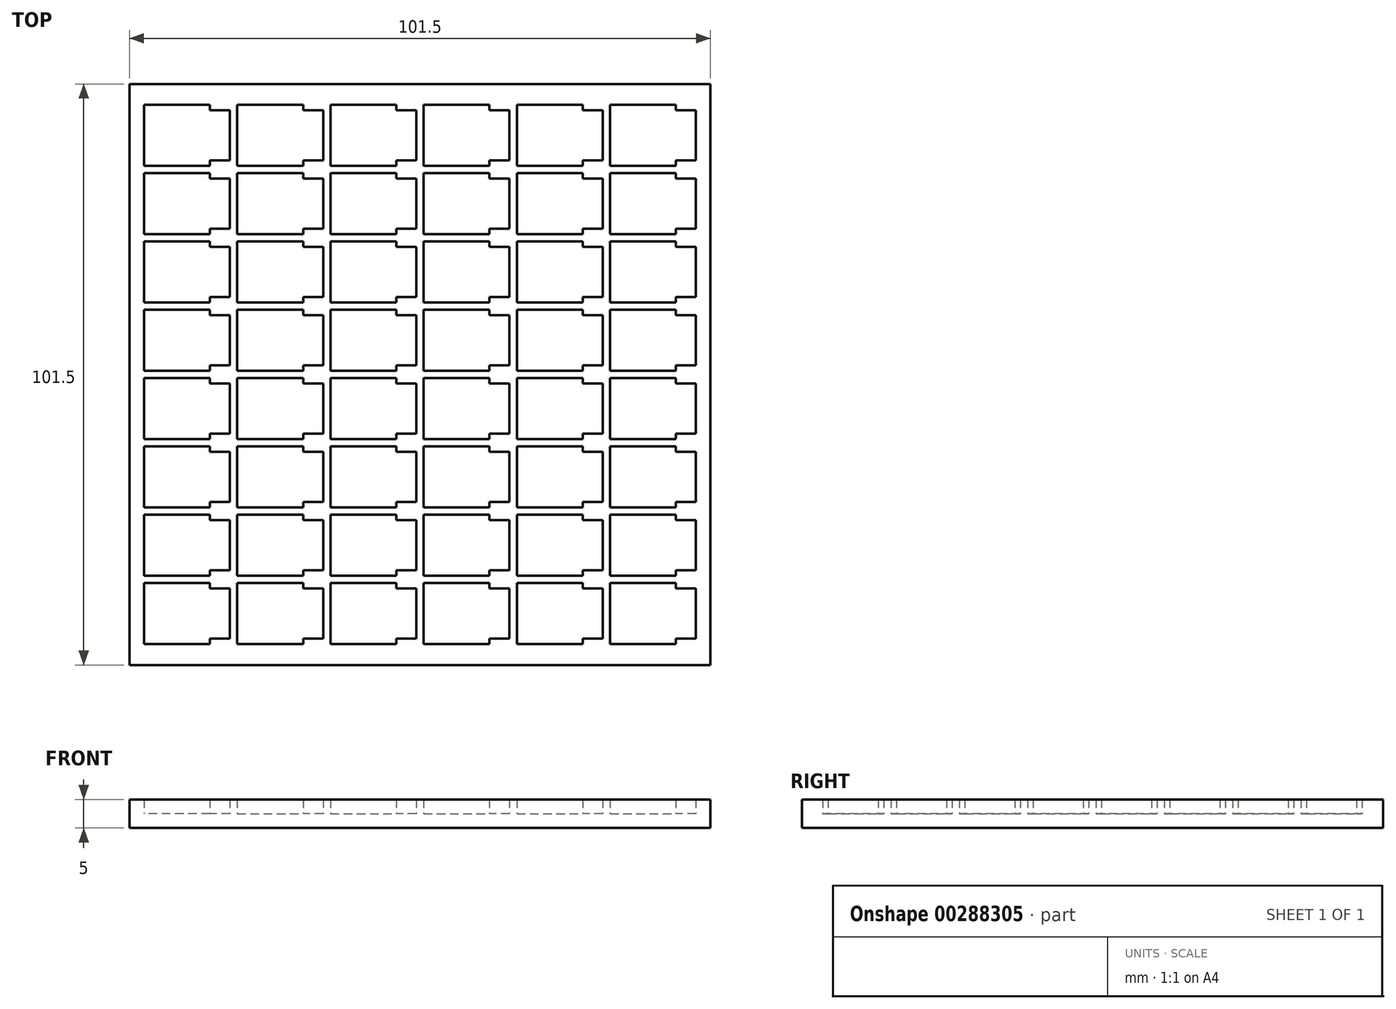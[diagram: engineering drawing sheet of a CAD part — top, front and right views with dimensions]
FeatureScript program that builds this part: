
annotation { "Feature Type Name" : "Feature", "Feature Type Description" : "" }
export const myFeature = defineFeature(function(context is Context, id is Id, definition is map)
    precondition{}
    {
        {
            var Q0;
            Q0=qCreatedBy(makeId("Top.planeOp"),FACE);
            var sketch = newSketch(context, id + "F0", { "sketchPlane" : qUnion([Q0])});
            skLineSegment(sketch, "E0.bottom", {"start": v(50.75, -50.75) * mm, "end": v(-50.75, -50.75) * mm});
            skLineSegment(sketch, "E0.top", {"start": v(50.75, 50.75) * mm, "end": v(-50.75, 50.75) * mm});
            skLineSegment(sketch, "E0.left", {"start": v(50.75, -50.75) * mm, "end": v(50.75, 50.75) * mm});
            skLineSegment(sketch, "E0.right", {"start": v(-50.75, -50.75) * mm, "end": v(-50.75, 50.75) * mm});
            skPoint(sketch, "E0.middle", {"position": v(0, 0) * mm});
            skLineSegment(sketch, "E1", {"start": v(-48.2, 47.12) * mm, "end": v(-48.2, 36.45) * mm});
            skLineSegment(sketch, "E2", {"start": v(-48.2, 36.45) * mm, "end": v(-36.7, 36.45) * mm});
            skLineSegment(sketch, "E3", {"start": v(-36.7, 36.45) * mm, "end": v(-36.7, 37.4) * mm});
            skLineSegment(sketch, "E4", {"start": v(-36.7, 37.4) * mm, "end": v(-33.2, 37.4) * mm});
            skLineSegment(sketch, "E5", {"start": v(-33.2, 37.4) * mm, "end": v(-33.2, 46.16) * mm});
            skLineSegment(sketch, "E6", {"start": v(-33.2, 46.16) * mm, "end": v(-36.7, 46.16) * mm});
            skLineSegment(sketch, "E7", {"start": v(-36.7, 46.16) * mm, "end": v(-36.7, 47.12) * mm});
            skLineSegment(sketch, "E8", {"start": v(-36.7, 47.12) * mm, "end": v(-48.2, 47.12) * mm});
            skLineSegment(sketch, "E9.0.1.0", {"start": v(-36.7, 24.5) * mm, "end": v(-36.7, 25.46) * mm});
            skLineSegment(sketch, "E9.0.1.1", {"start": v(-48.2, 24.5) * mm, "end": v(-36.7, 24.5) * mm});
            skLineSegment(sketch, "E9.0.1.2", {"start": v(-33.2, 25.46) * mm, "end": v(-33.2, 34.23) * mm});
            skLineSegment(sketch, "E9.0.1.3", {"start": v(-36.7, 34.23) * mm, "end": v(-36.7, 35.18) * mm});
            skLineSegment(sketch, "E9.0.1.4", {"start": v(-36.7, 25.46) * mm, "end": v(-33.2, 25.46) * mm});
            skLineSegment(sketch, "E9.0.1.5", {"start": v(-48.2, 35.18) * mm, "end": v(-48.2, 24.5) * mm});
            skLineSegment(sketch, "E9.0.1.6", {"start": v(-36.7, 35.18) * mm, "end": v(-48.2, 35.18) * mm});
            skLineSegment(sketch, "E9.0.1.7", {"start": v(-33.2, 34.23) * mm, "end": v(-36.7, 34.23) * mm});
            skLineSegment(sketch, "E9.0.2.0", {"start": v(-36.7, 12.57) * mm, "end": v(-36.7, 13.53) * mm});
            skLineSegment(sketch, "E9.0.2.1", {"start": v(-48.2, 12.57) * mm, "end": v(-36.7, 12.57) * mm});
            skLineSegment(sketch, "E9.0.2.2", {"start": v(-33.2, 13.53) * mm, "end": v(-33.2, 22.29) * mm});
            skLineSegment(sketch, "E9.0.2.3", {"start": v(-36.7, 22.29) * mm, "end": v(-36.7, 23.24) * mm});
            skLineSegment(sketch, "E9.0.2.4", {"start": v(-36.7, 13.53) * mm, "end": v(-33.2, 13.53) * mm});
            skLineSegment(sketch, "E9.0.2.5", {"start": v(-48.2, 23.24) * mm, "end": v(-48.2, 12.57) * mm});
            skLineSegment(sketch, "E9.0.2.6", {"start": v(-36.7, 23.24) * mm, "end": v(-48.2, 23.24) * mm});
            skLineSegment(sketch, "E9.0.2.7", {"start": v(-33.2, 22.29) * mm, "end": v(-36.7, 22.29) * mm});
            skLineSegment(sketch, "E9.0.3.0", {"start": v(-36.7, 0.63) * mm, "end": v(-36.7, 1.59) * mm});
            skLineSegment(sketch, "E9.0.3.1", {"start": v(-48.2, 0.63) * mm, "end": v(-36.7, 0.63) * mm});
            skLineSegment(sketch, "E9.0.3.2", {"start": v(-33.2, 1.59) * mm, "end": v(-33.2, 10.35) * mm});
            skLineSegment(sketch, "E9.0.3.3", {"start": v(-36.7, 10.35) * mm, "end": v(-36.7, 11.3) * mm});
            skLineSegment(sketch, "E9.0.3.4", {"start": v(-36.7, 1.59) * mm, "end": v(-33.2, 1.59) * mm});
            skLineSegment(sketch, "E9.0.3.5", {"start": v(-48.2, 11.3) * mm, "end": v(-48.2, 0.63) * mm});
            skLineSegment(sketch, "E9.0.3.6", {"start": v(-36.7, 11.3) * mm, "end": v(-48.2, 11.3) * mm});
            skLineSegment(sketch, "E9.0.3.7", {"start": v(-33.2, 10.35) * mm, "end": v(-36.7, 10.35) * mm});
            skLineSegment(sketch, "E9.0.4.0", {"start": v(-36.7, -11.3) * mm, "end": v(-36.7, -10.35) * mm});
            skLineSegment(sketch, "E9.0.4.1", {"start": v(-48.2, -11.3) * mm, "end": v(-36.7, -11.3) * mm});
            skLineSegment(sketch, "E9.0.4.2", {"start": v(-33.2, -10.35) * mm, "end": v(-33.2, -1.59) * mm});
            skLineSegment(sketch, "E9.0.4.3", {"start": v(-36.7, -1.59) * mm, "end": v(-36.7, -0.63) * mm});
            skLineSegment(sketch, "E9.0.4.4", {"start": v(-36.7, -10.35) * mm, "end": v(-33.2, -10.35) * mm});
            skLineSegment(sketch, "E9.0.4.5", {"start": v(-48.2, -0.63) * mm, "end": v(-48.2, -11.3) * mm});
            skLineSegment(sketch, "E9.0.4.6", {"start": v(-36.7, -0.63) * mm, "end": v(-48.2, -0.63) * mm});
            skLineSegment(sketch, "E9.0.4.7", {"start": v(-33.2, -1.59) * mm, "end": v(-36.7, -1.59) * mm});
            skLineSegment(sketch, "E9.0.5.0", {"start": v(-36.7, -23.24) * mm, "end": v(-36.7, -22.29) * mm});
            skLineSegment(sketch, "E9.0.5.1", {"start": v(-48.2, -23.24) * mm, "end": v(-36.7, -23.24) * mm});
            skLineSegment(sketch, "E9.0.5.2", {"start": v(-33.2, -22.29) * mm, "end": v(-33.2, -13.53) * mm});
            skLineSegment(sketch, "E9.0.5.3", {"start": v(-36.7, -13.53) * mm, "end": v(-36.7, -12.57) * mm});
            skLineSegment(sketch, "E9.0.5.4", {"start": v(-36.7, -22.29) * mm, "end": v(-33.2, -22.29) * mm});
            skLineSegment(sketch, "E9.0.5.5", {"start": v(-48.2, -12.57) * mm, "end": v(-48.2, -23.24) * mm});
            skLineSegment(sketch, "E9.0.5.6", {"start": v(-36.7, -12.57) * mm, "end": v(-48.2, -12.57) * mm});
            skLineSegment(sketch, "E9.0.5.7", {"start": v(-33.2, -13.53) * mm, "end": v(-36.7, -13.53) * mm});
            skLineSegment(sketch, "E9.0.6.0", {"start": v(-36.7, -35.18) * mm, "end": v(-36.7, -34.23) * mm});
            skLineSegment(sketch, "E9.0.6.1", {"start": v(-48.2, -35.18) * mm, "end": v(-36.7, -35.18) * mm});
            skLineSegment(sketch, "E9.0.6.2", {"start": v(-33.2, -34.23) * mm, "end": v(-33.2, -25.46) * mm});
            skLineSegment(sketch, "E9.0.6.3", {"start": v(-36.7, -25.46) * mm, "end": v(-36.7, -24.51) * mm});
            skLineSegment(sketch, "E9.0.6.4", {"start": v(-36.7, -34.23) * mm, "end": v(-33.2, -34.23) * mm});
            skLineSegment(sketch, "E9.0.6.5", {"start": v(-48.2, -24.51) * mm, "end": v(-48.2, -35.18) * mm});
            skLineSegment(sketch, "E9.0.6.6", {"start": v(-36.7, -24.51) * mm, "end": v(-48.2, -24.51) * mm});
            skLineSegment(sketch, "E9.0.6.7", {"start": v(-33.2, -25.46) * mm, "end": v(-36.7, -25.46) * mm});
            skLineSegment(sketch, "E9.0.7.0", {"start": v(-36.7, -47.12) * mm, "end": v(-36.7, -46.16) * mm});
            skLineSegment(sketch, "E9.0.7.1", {"start": v(-48.2, -47.12) * mm, "end": v(-36.7, -47.12) * mm});
            skLineSegment(sketch, "E9.0.7.2", {"start": v(-33.2, -46.16) * mm, "end": v(-33.2, -37.4) * mm});
            skLineSegment(sketch, "E9.0.7.3", {"start": v(-36.7, -37.4) * mm, "end": v(-36.7, -36.45) * mm});
            skLineSegment(sketch, "E9.0.7.4", {"start": v(-36.7, -46.16) * mm, "end": v(-33.2, -46.16) * mm});
            skLineSegment(sketch, "E9.0.7.5", {"start": v(-48.2, -36.45) * mm, "end": v(-48.2, -47.12) * mm});
            skLineSegment(sketch, "E9.0.7.6", {"start": v(-36.7, -36.45) * mm, "end": v(-48.2, -36.45) * mm});
            skLineSegment(sketch, "E9.0.7.7", {"start": v(-33.2, -37.4) * mm, "end": v(-36.7, -37.4) * mm});
            skLineSegment(sketch, "E9.1.0.0", {"start": v(-20.42, 36.45) * mm, "end": v(-20.42, 37.4) * mm});
            skLineSegment(sketch, "E9.1.0.1", {"start": v(-31.92, 36.45) * mm, "end": v(-20.42, 36.45) * mm});
            skLineSegment(sketch, "E9.1.0.2", {"start": v(-16.92, 37.4) * mm, "end": v(-16.92, 46.16) * mm});
            skLineSegment(sketch, "E9.1.0.3", {"start": v(-20.42, 46.16) * mm, "end": v(-20.42, 47.12) * mm});
            skLineSegment(sketch, "E9.1.0.4", {"start": v(-20.42, 37.4) * mm, "end": v(-16.92, 37.4) * mm});
            skLineSegment(sketch, "E9.1.0.5", {"start": v(-31.92, 47.12) * mm, "end": v(-31.92, 36.45) * mm});
            skLineSegment(sketch, "E9.1.0.6", {"start": v(-20.42, 47.12) * mm, "end": v(-31.92, 47.12) * mm});
            skLineSegment(sketch, "E9.1.0.7", {"start": v(-16.92, 46.16) * mm, "end": v(-20.42, 46.16) * mm});
            skLineSegment(sketch, "E9.1.1.0", {"start": v(-20.42, 24.5) * mm, "end": v(-20.42, 25.46) * mm});
            skLineSegment(sketch, "E9.1.1.1", {"start": v(-31.92, 24.5) * mm, "end": v(-20.42, 24.5) * mm});
            skLineSegment(sketch, "E9.1.1.2", {"start": v(-16.92, 25.46) * mm, "end": v(-16.92, 34.23) * mm});
            skLineSegment(sketch, "E9.1.1.3", {"start": v(-20.42, 34.23) * mm, "end": v(-20.42, 35.18) * mm});
            skLineSegment(sketch, "E9.1.1.4", {"start": v(-20.42, 25.46) * mm, "end": v(-16.92, 25.46) * mm});
            skLineSegment(sketch, "E9.1.1.5", {"start": v(-31.92, 35.18) * mm, "end": v(-31.92, 24.5) * mm});
            skLineSegment(sketch, "E9.1.1.6", {"start": v(-20.42, 35.18) * mm, "end": v(-31.92, 35.18) * mm});
            skLineSegment(sketch, "E9.1.1.7", {"start": v(-16.92, 34.23) * mm, "end": v(-20.42, 34.23) * mm});
            skLineSegment(sketch, "E9.1.2.0", {"start": v(-20.42, 12.57) * mm, "end": v(-20.42, 13.53) * mm});
            skLineSegment(sketch, "E9.1.2.1", {"start": v(-31.92, 12.57) * mm, "end": v(-20.42, 12.57) * mm});
            skLineSegment(sketch, "E9.1.2.2", {"start": v(-16.92, 13.53) * mm, "end": v(-16.92, 22.29) * mm});
            skLineSegment(sketch, "E9.1.2.3", {"start": v(-20.42, 22.29) * mm, "end": v(-20.42, 23.24) * mm});
            skLineSegment(sketch, "E9.1.2.4", {"start": v(-20.42, 13.53) * mm, "end": v(-16.92, 13.53) * mm});
            skLineSegment(sketch, "E9.1.2.5", {"start": v(-31.92, 23.24) * mm, "end": v(-31.92, 12.57) * mm});
            skLineSegment(sketch, "E9.1.2.6", {"start": v(-20.42, 23.24) * mm, "end": v(-31.92, 23.24) * mm});
            skLineSegment(sketch, "E9.1.2.7", {"start": v(-16.92, 22.29) * mm, "end": v(-20.42, 22.29) * mm});
            skLineSegment(sketch, "E9.1.3.0", {"start": v(-20.42, 0.63) * mm, "end": v(-20.42, 1.59) * mm});
            skLineSegment(sketch, "E9.1.3.1", {"start": v(-31.92, 0.63) * mm, "end": v(-20.42, 0.63) * mm});
            skLineSegment(sketch, "E9.1.3.2", {"start": v(-16.92, 1.59) * mm, "end": v(-16.92, 10.35) * mm});
            skLineSegment(sketch, "E9.1.3.3", {"start": v(-20.42, 10.35) * mm, "end": v(-20.42, 11.3) * mm});
            skLineSegment(sketch, "E9.1.3.4", {"start": v(-20.42, 1.59) * mm, "end": v(-16.92, 1.59) * mm});
            skLineSegment(sketch, "E9.1.3.5", {"start": v(-31.92, 11.3) * mm, "end": v(-31.92, 0.63) * mm});
            skLineSegment(sketch, "E9.1.3.6", {"start": v(-20.42, 11.3) * mm, "end": v(-31.92, 11.3) * mm});
            skLineSegment(sketch, "E9.1.3.7", {"start": v(-16.92, 10.35) * mm, "end": v(-20.42, 10.35) * mm});
            skLineSegment(sketch, "E9.1.4.0", {"start": v(-20.42, -11.3) * mm, "end": v(-20.42, -10.35) * mm});
            skLineSegment(sketch, "E9.1.4.1", {"start": v(-31.92, -11.3) * mm, "end": v(-20.42, -11.3) * mm});
            skLineSegment(sketch, "E9.1.4.2", {"start": v(-16.92, -10.35) * mm, "end": v(-16.92, -1.59) * mm});
            skLineSegment(sketch, "E9.1.4.3", {"start": v(-20.42, -1.59) * mm, "end": v(-20.42, -0.63) * mm});
            skLineSegment(sketch, "E9.1.4.4", {"start": v(-20.42, -10.35) * mm, "end": v(-16.92, -10.35) * mm});
            skLineSegment(sketch, "E9.1.4.5", {"start": v(-31.92, -0.63) * mm, "end": v(-31.92, -11.3) * mm});
            skLineSegment(sketch, "E9.1.4.6", {"start": v(-20.42, -0.63) * mm, "end": v(-31.92, -0.63) * mm});
            skLineSegment(sketch, "E9.1.4.7", {"start": v(-16.92, -1.59) * mm, "end": v(-20.42, -1.59) * mm});
            skLineSegment(sketch, "E9.1.5.0", {"start": v(-20.42, -23.24) * mm, "end": v(-20.42, -22.29) * mm});
            skLineSegment(sketch, "E9.1.5.1", {"start": v(-31.92, -23.24) * mm, "end": v(-20.42, -23.24) * mm});
            skLineSegment(sketch, "E9.1.5.2", {"start": v(-16.92, -22.29) * mm, "end": v(-16.92, -13.53) * mm});
            skLineSegment(sketch, "E9.1.5.3", {"start": v(-20.42, -13.53) * mm, "end": v(-20.42, -12.57) * mm});
            skLineSegment(sketch, "E9.1.5.4", {"start": v(-20.42, -22.29) * mm, "end": v(-16.92, -22.29) * mm});
            skLineSegment(sketch, "E9.1.5.5", {"start": v(-31.92, -12.57) * mm, "end": v(-31.92, -23.24) * mm});
            skLineSegment(sketch, "E9.1.5.6", {"start": v(-20.42, -12.57) * mm, "end": v(-31.92, -12.57) * mm});
            skLineSegment(sketch, "E9.1.5.7", {"start": v(-16.92, -13.53) * mm, "end": v(-20.42, -13.53) * mm});
            skLineSegment(sketch, "E9.1.6.0", {"start": v(-20.42, -35.18) * mm, "end": v(-20.42, -34.23) * mm});
            skLineSegment(sketch, "E9.1.6.1", {"start": v(-31.92, -35.18) * mm, "end": v(-20.42, -35.18) * mm});
            skLineSegment(sketch, "E9.1.6.2", {"start": v(-16.92, -34.23) * mm, "end": v(-16.92, -25.46) * mm});
            skLineSegment(sketch, "E9.1.6.3", {"start": v(-20.42, -25.46) * mm, "end": v(-20.42, -24.51) * mm});
            skLineSegment(sketch, "E9.1.6.4", {"start": v(-20.42, -34.23) * mm, "end": v(-16.92, -34.23) * mm});
            skLineSegment(sketch, "E9.1.6.5", {"start": v(-31.92, -24.51) * mm, "end": v(-31.92, -35.18) * mm});
            skLineSegment(sketch, "E9.1.6.6", {"start": v(-20.42, -24.51) * mm, "end": v(-31.92, -24.51) * mm});
            skLineSegment(sketch, "E9.1.6.7", {"start": v(-16.92, -25.46) * mm, "end": v(-20.42, -25.46) * mm});
            skLineSegment(sketch, "E9.1.7.0", {"start": v(-20.42, -47.12) * mm, "end": v(-20.42, -46.16) * mm});
            skLineSegment(sketch, "E9.1.7.1", {"start": v(-31.92, -47.12) * mm, "end": v(-20.42, -47.12) * mm});
            skLineSegment(sketch, "E9.1.7.2", {"start": v(-16.92, -46.16) * mm, "end": v(-16.92, -37.4) * mm});
            skLineSegment(sketch, "E9.1.7.3", {"start": v(-20.42, -37.4) * mm, "end": v(-20.42, -36.45) * mm});
            skLineSegment(sketch, "E9.1.7.4", {"start": v(-20.42, -46.16) * mm, "end": v(-16.92, -46.16) * mm});
            skLineSegment(sketch, "E9.1.7.5", {"start": v(-31.92, -36.45) * mm, "end": v(-31.92, -47.12) * mm});
            skLineSegment(sketch, "E9.1.7.6", {"start": v(-20.42, -36.45) * mm, "end": v(-31.92, -36.45) * mm});
            skLineSegment(sketch, "E9.1.7.7", {"start": v(-16.92, -37.4) * mm, "end": v(-20.42, -37.4) * mm});
            skLineSegment(sketch, "E9.2.0.0", {"start": v(-4.13, 36.45) * mm, "end": v(-4.13, 37.4) * mm});
            skLineSegment(sketch, "E9.2.0.1", {"start": v(-15.63, 36.45) * mm, "end": v(-4.13, 36.45) * mm});
            skLineSegment(sketch, "E9.2.0.2", {"start": v(-0.63, 37.4) * mm, "end": v(-0.63, 46.16) * mm});
            skLineSegment(sketch, "E9.2.0.3", {"start": v(-4.13, 46.16) * mm, "end": v(-4.13, 47.12) * mm});
            skLineSegment(sketch, "E9.2.0.4", {"start": v(-4.13, 37.4) * mm, "end": v(-0.63, 37.4) * mm});
            skLineSegment(sketch, "E9.2.0.5", {"start": v(-15.63, 47.12) * mm, "end": v(-15.63, 36.45) * mm});
            skLineSegment(sketch, "E9.2.0.6", {"start": v(-4.13, 47.12) * mm, "end": v(-15.63, 47.12) * mm});
            skLineSegment(sketch, "E9.2.0.7", {"start": v(-0.63, 46.16) * mm, "end": v(-4.13, 46.16) * mm});
            skLineSegment(sketch, "E9.2.1.0", {"start": v(-4.13, 24.5) * mm, "end": v(-4.13, 25.46) * mm});
            skLineSegment(sketch, "E9.2.1.1", {"start": v(-15.63, 24.5) * mm, "end": v(-4.13, 24.5) * mm});
            skLineSegment(sketch, "E9.2.1.2", {"start": v(-0.63, 25.46) * mm, "end": v(-0.63, 34.23) * mm});
            skLineSegment(sketch, "E9.2.1.3", {"start": v(-4.13, 34.23) * mm, "end": v(-4.13, 35.18) * mm});
            skLineSegment(sketch, "E9.2.1.4", {"start": v(-4.13, 25.46) * mm, "end": v(-0.63, 25.46) * mm});
            skLineSegment(sketch, "E9.2.1.5", {"start": v(-15.63, 35.18) * mm, "end": v(-15.63, 24.5) * mm});
            skLineSegment(sketch, "E9.2.1.6", {"start": v(-4.13, 35.18) * mm, "end": v(-15.63, 35.18) * mm});
            skLineSegment(sketch, "E9.2.1.7", {"start": v(-0.63, 34.23) * mm, "end": v(-4.13, 34.23) * mm});
            skLineSegment(sketch, "E9.2.2.0", {"start": v(-4.13, 12.57) * mm, "end": v(-4.13, 13.53) * mm});
            skLineSegment(sketch, "E9.2.2.1", {"start": v(-15.63, 12.57) * mm, "end": v(-4.13, 12.57) * mm});
            skLineSegment(sketch, "E9.2.2.2", {"start": v(-0.63, 13.53) * mm, "end": v(-0.63, 22.29) * mm});
            skLineSegment(sketch, "E9.2.2.3", {"start": v(-4.13, 22.29) * mm, "end": v(-4.13, 23.24) * mm});
            skLineSegment(sketch, "E9.2.2.4", {"start": v(-4.13, 13.53) * mm, "end": v(-0.63, 13.53) * mm});
            skLineSegment(sketch, "E9.2.2.5", {"start": v(-15.63, 23.24) * mm, "end": v(-15.63, 12.57) * mm});
            skLineSegment(sketch, "E9.2.2.6", {"start": v(-4.13, 23.24) * mm, "end": v(-15.63, 23.24) * mm});
            skLineSegment(sketch, "E9.2.2.7", {"start": v(-0.63, 22.29) * mm, "end": v(-4.13, 22.29) * mm});
            skLineSegment(sketch, "E9.2.3.0", {"start": v(-4.13, 0.63) * mm, "end": v(-4.13, 1.59) * mm});
            skLineSegment(sketch, "E9.2.3.1", {"start": v(-15.63, 0.63) * mm, "end": v(-4.13, 0.63) * mm});
            skLineSegment(sketch, "E9.2.3.2", {"start": v(-0.63, 1.59) * mm, "end": v(-0.63, 10.35) * mm});
            skLineSegment(sketch, "E9.2.3.3", {"start": v(-4.13, 10.35) * mm, "end": v(-4.13, 11.3) * mm});
            skLineSegment(sketch, "E9.2.3.4", {"start": v(-4.13, 1.59) * mm, "end": v(-0.63, 1.59) * mm});
            skLineSegment(sketch, "E9.2.3.5", {"start": v(-15.63, 11.3) * mm, "end": v(-15.63, 0.63) * mm});
            skLineSegment(sketch, "E9.2.3.6", {"start": v(-4.13, 11.3) * mm, "end": v(-15.63, 11.3) * mm});
            skLineSegment(sketch, "E9.2.3.7", {"start": v(-0.63, 10.35) * mm, "end": v(-4.13, 10.35) * mm});
            skLineSegment(sketch, "E9.2.4.0", {"start": v(-4.13, -11.3) * mm, "end": v(-4.13, -10.35) * mm});
            skLineSegment(sketch, "E9.2.4.1", {"start": v(-15.63, -11.3) * mm, "end": v(-4.13, -11.3) * mm});
            skLineSegment(sketch, "E9.2.4.2", {"start": v(-0.63, -10.35) * mm, "end": v(-0.63, -1.59) * mm});
            skLineSegment(sketch, "E9.2.4.3", {"start": v(-4.13, -1.59) * mm, "end": v(-4.13, -0.63) * mm});
            skLineSegment(sketch, "E9.2.4.4", {"start": v(-4.13, -10.35) * mm, "end": v(-0.63, -10.35) * mm});
            skLineSegment(sketch, "E9.2.4.5", {"start": v(-15.63, -0.63) * mm, "end": v(-15.63, -11.3) * mm});
            skLineSegment(sketch, "E9.2.4.6", {"start": v(-4.13, -0.63) * mm, "end": v(-15.63, -0.63) * mm});
            skLineSegment(sketch, "E9.2.4.7", {"start": v(-0.63, -1.59) * mm, "end": v(-4.13, -1.59) * mm});
            skLineSegment(sketch, "E9.2.5.0", {"start": v(-4.13, -23.24) * mm, "end": v(-4.13, -22.29) * mm});
            skLineSegment(sketch, "E9.2.5.1", {"start": v(-15.63, -23.24) * mm, "end": v(-4.13, -23.24) * mm});
            skLineSegment(sketch, "E9.2.5.2", {"start": v(-0.63, -22.29) * mm, "end": v(-0.63, -13.53) * mm});
            skLineSegment(sketch, "E9.2.5.3", {"start": v(-4.13, -13.53) * mm, "end": v(-4.13, -12.57) * mm});
            skLineSegment(sketch, "E9.2.5.4", {"start": v(-4.13, -22.29) * mm, "end": v(-0.63, -22.29) * mm});
            skLineSegment(sketch, "E9.2.5.5", {"start": v(-15.63, -12.57) * mm, "end": v(-15.63, -23.24) * mm});
            skLineSegment(sketch, "E9.2.5.6", {"start": v(-4.13, -12.57) * mm, "end": v(-15.63, -12.57) * mm});
            skLineSegment(sketch, "E9.2.5.7", {"start": v(-0.63, -13.53) * mm, "end": v(-4.13, -13.53) * mm});
            skLineSegment(sketch, "E9.2.6.0", {"start": v(-4.13, -35.18) * mm, "end": v(-4.13, -34.23) * mm});
            skLineSegment(sketch, "E9.2.6.1", {"start": v(-15.63, -35.18) * mm, "end": v(-4.13, -35.18) * mm});
            skLineSegment(sketch, "E9.2.6.2", {"start": v(-0.63, -34.23) * mm, "end": v(-0.63, -25.46) * mm});
            skLineSegment(sketch, "E9.2.6.3", {"start": v(-4.13, -25.46) * mm, "end": v(-4.13, -24.51) * mm});
            skLineSegment(sketch, "E9.2.6.4", {"start": v(-4.13, -34.23) * mm, "end": v(-0.63, -34.23) * mm});
            skLineSegment(sketch, "E9.2.6.5", {"start": v(-15.63, -24.51) * mm, "end": v(-15.63, -35.18) * mm});
            skLineSegment(sketch, "E9.2.6.6", {"start": v(-4.13, -24.51) * mm, "end": v(-15.63, -24.51) * mm});
            skLineSegment(sketch, "E9.2.6.7", {"start": v(-0.63, -25.46) * mm, "end": v(-4.13, -25.46) * mm});
            skLineSegment(sketch, "E9.2.7.0", {"start": v(-4.13, -47.12) * mm, "end": v(-4.13, -46.16) * mm});
            skLineSegment(sketch, "E9.2.7.1", {"start": v(-15.63, -47.12) * mm, "end": v(-4.13, -47.12) * mm});
            skLineSegment(sketch, "E9.2.7.2", {"start": v(-0.63, -46.16) * mm, "end": v(-0.63, -37.4) * mm});
            skLineSegment(sketch, "E9.2.7.3", {"start": v(-4.13, -37.4) * mm, "end": v(-4.13, -36.45) * mm});
            skLineSegment(sketch, "E9.2.7.4", {"start": v(-4.13, -46.16) * mm, "end": v(-0.63, -46.16) * mm});
            skLineSegment(sketch, "E9.2.7.5", {"start": v(-15.63, -36.45) * mm, "end": v(-15.63, -47.12) * mm});
            skLineSegment(sketch, "E9.2.7.6", {"start": v(-4.13, -36.45) * mm, "end": v(-15.63, -36.45) * mm});
            skLineSegment(sketch, "E9.2.7.7", {"start": v(-0.63, -37.4) * mm, "end": v(-4.13, -37.4) * mm});
            skLineSegment(sketch, "E9.3.0.0", {"start": v(12.15, 36.45) * mm, "end": v(12.15, 37.4) * mm});
            skLineSegment(sketch, "E9.3.0.1", {"start": v(0.65, 36.45) * mm, "end": v(12.15, 36.45) * mm});
            skLineSegment(sketch, "E9.3.0.2", {"start": v(15.65, 37.4) * mm, "end": v(15.65, 46.16) * mm});
            skLineSegment(sketch, "E9.3.0.3", {"start": v(12.15, 46.16) * mm, "end": v(12.15, 47.12) * mm});
            skLineSegment(sketch, "E9.3.0.4", {"start": v(12.15, 37.4) * mm, "end": v(15.65, 37.4) * mm});
            skLineSegment(sketch, "E9.3.0.5", {"start": v(0.65, 47.12) * mm, "end": v(0.65, 36.45) * mm});
            skLineSegment(sketch, "E9.3.0.6", {"start": v(12.15, 47.12) * mm, "end": v(0.65, 47.12) * mm});
            skLineSegment(sketch, "E9.3.0.7", {"start": v(15.65, 46.16) * mm, "end": v(12.15, 46.16) * mm});
            skLineSegment(sketch, "E9.3.1.0", {"start": v(12.15, 24.5) * mm, "end": v(12.15, 25.46) * mm});
            skLineSegment(sketch, "E9.3.1.1", {"start": v(0.65, 24.5) * mm, "end": v(12.15, 24.5) * mm});
            skLineSegment(sketch, "E9.3.1.2", {"start": v(15.65, 25.46) * mm, "end": v(15.65, 34.23) * mm});
            skLineSegment(sketch, "E9.3.1.3", {"start": v(12.15, 34.23) * mm, "end": v(12.15, 35.18) * mm});
            skLineSegment(sketch, "E9.3.1.4", {"start": v(12.15, 25.46) * mm, "end": v(15.65, 25.46) * mm});
            skLineSegment(sketch, "E9.3.1.5", {"start": v(0.65, 35.18) * mm, "end": v(0.65, 24.5) * mm});
            skLineSegment(sketch, "E9.3.1.6", {"start": v(12.15, 35.18) * mm, "end": v(0.65, 35.18) * mm});
            skLineSegment(sketch, "E9.3.1.7", {"start": v(15.65, 34.23) * mm, "end": v(12.15, 34.23) * mm});
            skLineSegment(sketch, "E9.3.2.0", {"start": v(12.15, 12.57) * mm, "end": v(12.15, 13.53) * mm});
            skLineSegment(sketch, "E9.3.2.1", {"start": v(0.65, 12.57) * mm, "end": v(12.15, 12.57) * mm});
            skLineSegment(sketch, "E9.3.2.2", {"start": v(15.65, 13.53) * mm, "end": v(15.65, 22.29) * mm});
            skLineSegment(sketch, "E9.3.2.3", {"start": v(12.15, 22.29) * mm, "end": v(12.15, 23.24) * mm});
            skLineSegment(sketch, "E9.3.2.4", {"start": v(12.15, 13.53) * mm, "end": v(15.65, 13.53) * mm});
            skLineSegment(sketch, "E9.3.2.5", {"start": v(0.65, 23.24) * mm, "end": v(0.65, 12.57) * mm});
            skLineSegment(sketch, "E9.3.2.6", {"start": v(12.15, 23.24) * mm, "end": v(0.65, 23.24) * mm});
            skLineSegment(sketch, "E9.3.2.7", {"start": v(15.65, 22.29) * mm, "end": v(12.15, 22.29) * mm});
            skLineSegment(sketch, "E9.3.3.0", {"start": v(12.15, 0.63) * mm, "end": v(12.15, 1.59) * mm});
            skLineSegment(sketch, "E9.3.3.1", {"start": v(0.65, 0.63) * mm, "end": v(12.15, 0.63) * mm});
            skLineSegment(sketch, "E9.3.3.2", {"start": v(15.65, 1.59) * mm, "end": v(15.65, 10.35) * mm});
            skLineSegment(sketch, "E9.3.3.3", {"start": v(12.15, 10.35) * mm, "end": v(12.15, 11.3) * mm});
            skLineSegment(sketch, "E9.3.3.4", {"start": v(12.15, 1.59) * mm, "end": v(15.65, 1.59) * mm});
            skLineSegment(sketch, "E9.3.3.5", {"start": v(0.65, 11.3) * mm, "end": v(0.65, 0.63) * mm});
            skLineSegment(sketch, "E9.3.3.6", {"start": v(12.15, 11.3) * mm, "end": v(0.65, 11.3) * mm});
            skLineSegment(sketch, "E9.3.3.7", {"start": v(15.65, 10.35) * mm, "end": v(12.15, 10.35) * mm});
            skLineSegment(sketch, "E9.3.4.0", {"start": v(12.15, -11.3) * mm, "end": v(12.15, -10.35) * mm});
            skLineSegment(sketch, "E9.3.4.1", {"start": v(0.65, -11.3) * mm, "end": v(12.15, -11.3) * mm});
            skLineSegment(sketch, "E9.3.4.2", {"start": v(15.65, -10.35) * mm, "end": v(15.65, -1.59) * mm});
            skLineSegment(sketch, "E9.3.4.3", {"start": v(12.15, -1.59) * mm, "end": v(12.15, -0.63) * mm});
            skLineSegment(sketch, "E9.3.4.4", {"start": v(12.15, -10.35) * mm, "end": v(15.65, -10.35) * mm});
            skLineSegment(sketch, "E9.3.4.5", {"start": v(0.65, -0.63) * mm, "end": v(0.65, -11.3) * mm});
            skLineSegment(sketch, "E9.3.4.6", {"start": v(12.15, -0.63) * mm, "end": v(0.65, -0.63) * mm});
            skLineSegment(sketch, "E9.3.4.7", {"start": v(15.65, -1.59) * mm, "end": v(12.15, -1.59) * mm});
            skLineSegment(sketch, "E9.3.5.0", {"start": v(12.15, -23.24) * mm, "end": v(12.15, -22.29) * mm});
            skLineSegment(sketch, "E9.3.5.1", {"start": v(0.65, -23.24) * mm, "end": v(12.15, -23.24) * mm});
            skLineSegment(sketch, "E9.3.5.2", {"start": v(15.65, -22.29) * mm, "end": v(15.65, -13.53) * mm});
            skLineSegment(sketch, "E9.3.5.3", {"start": v(12.15, -13.53) * mm, "end": v(12.15, -12.57) * mm});
            skLineSegment(sketch, "E9.3.5.4", {"start": v(12.15, -22.29) * mm, "end": v(15.65, -22.29) * mm});
            skLineSegment(sketch, "E9.3.5.5", {"start": v(0.65, -12.57) * mm, "end": v(0.65, -23.24) * mm});
            skLineSegment(sketch, "E9.3.5.6", {"start": v(12.15, -12.57) * mm, "end": v(0.65, -12.57) * mm});
            skLineSegment(sketch, "E9.3.5.7", {"start": v(15.65, -13.53) * mm, "end": v(12.15, -13.53) * mm});
            skLineSegment(sketch, "E9.3.6.0", {"start": v(12.15, -35.18) * mm, "end": v(12.15, -34.23) * mm});
            skLineSegment(sketch, "E9.3.6.1", {"start": v(0.65, -35.18) * mm, "end": v(12.15, -35.18) * mm});
            skLineSegment(sketch, "E9.3.6.2", {"start": v(15.65, -34.23) * mm, "end": v(15.65, -25.46) * mm});
            skLineSegment(sketch, "E9.3.6.3", {"start": v(12.15, -25.46) * mm, "end": v(12.15, -24.51) * mm});
            skLineSegment(sketch, "E9.3.6.4", {"start": v(12.15, -34.23) * mm, "end": v(15.65, -34.23) * mm});
            skLineSegment(sketch, "E9.3.6.5", {"start": v(0.65, -24.51) * mm, "end": v(0.65, -35.18) * mm});
            skLineSegment(sketch, "E9.3.6.6", {"start": v(12.15, -24.51) * mm, "end": v(0.65, -24.51) * mm});
            skLineSegment(sketch, "E9.3.6.7", {"start": v(15.65, -25.46) * mm, "end": v(12.15, -25.46) * mm});
            skLineSegment(sketch, "E9.3.7.0", {"start": v(12.15, -47.12) * mm, "end": v(12.15, -46.16) * mm});
            skLineSegment(sketch, "E9.3.7.1", {"start": v(0.65, -47.12) * mm, "end": v(12.15, -47.12) * mm});
            skLineSegment(sketch, "E9.3.7.2", {"start": v(15.65, -46.16) * mm, "end": v(15.65, -37.4) * mm});
            skLineSegment(sketch, "E9.3.7.3", {"start": v(12.15, -37.4) * mm, "end": v(12.15, -36.45) * mm});
            skLineSegment(sketch, "E9.3.7.4", {"start": v(12.15, -46.16) * mm, "end": v(15.65, -46.16) * mm});
            skLineSegment(sketch, "E9.3.7.5", {"start": v(0.65, -36.45) * mm, "end": v(0.65, -47.12) * mm});
            skLineSegment(sketch, "E9.3.7.6", {"start": v(12.15, -36.45) * mm, "end": v(0.65, -36.45) * mm});
            skLineSegment(sketch, "E9.3.7.7", {"start": v(15.65, -37.4) * mm, "end": v(12.15, -37.4) * mm});
            skLineSegment(sketch, "E9.4.0.0", {"start": v(28.43, 36.45) * mm, "end": v(28.43, 37.4) * mm});
            skLineSegment(sketch, "E9.4.0.1", {"start": v(16.93, 36.45) * mm, "end": v(28.43, 36.45) * mm});
            skLineSegment(sketch, "E9.4.0.2", {"start": v(31.93, 37.4) * mm, "end": v(31.93, 46.16) * mm});
            skLineSegment(sketch, "E9.4.0.3", {"start": v(28.43, 46.16) * mm, "end": v(28.43, 47.12) * mm});
            skLineSegment(sketch, "E9.4.0.4", {"start": v(28.43, 37.4) * mm, "end": v(31.93, 37.4) * mm});
            skLineSegment(sketch, "E9.4.0.5", {"start": v(16.93, 47.12) * mm, "end": v(16.93, 36.45) * mm});
            skLineSegment(sketch, "E9.4.0.6", {"start": v(28.43, 47.12) * mm, "end": v(16.93, 47.12) * mm});
            skLineSegment(sketch, "E9.4.0.7", {"start": v(31.93, 46.16) * mm, "end": v(28.43, 46.16) * mm});
            skLineSegment(sketch, "E9.4.1.0", {"start": v(28.43, 24.5) * mm, "end": v(28.43, 25.46) * mm});
            skLineSegment(sketch, "E9.4.1.1", {"start": v(16.93, 24.5) * mm, "end": v(28.43, 24.5) * mm});
            skLineSegment(sketch, "E9.4.1.2", {"start": v(31.93, 25.46) * mm, "end": v(31.93, 34.23) * mm});
            skLineSegment(sketch, "E9.4.1.3", {"start": v(28.43, 34.23) * mm, "end": v(28.43, 35.18) * mm});
            skLineSegment(sketch, "E9.4.1.4", {"start": v(28.43, 25.46) * mm, "end": v(31.93, 25.46) * mm});
            skLineSegment(sketch, "E9.4.1.5", {"start": v(16.93, 35.18) * mm, "end": v(16.93, 24.5) * mm});
            skLineSegment(sketch, "E9.4.1.6", {"start": v(28.43, 35.18) * mm, "end": v(16.93, 35.18) * mm});
            skLineSegment(sketch, "E9.4.1.7", {"start": v(31.93, 34.23) * mm, "end": v(28.43, 34.23) * mm});
            skLineSegment(sketch, "E9.4.2.0", {"start": v(28.43, 12.57) * mm, "end": v(28.43, 13.53) * mm});
            skLineSegment(sketch, "E9.4.2.1", {"start": v(16.93, 12.57) * mm, "end": v(28.43, 12.57) * mm});
            skLineSegment(sketch, "E9.4.2.2", {"start": v(31.93, 13.53) * mm, "end": v(31.93, 22.29) * mm});
            skLineSegment(sketch, "E9.4.2.3", {"start": v(28.43, 22.29) * mm, "end": v(28.43, 23.24) * mm});
            skLineSegment(sketch, "E9.4.2.4", {"start": v(28.43, 13.53) * mm, "end": v(31.93, 13.53) * mm});
            skLineSegment(sketch, "E9.4.2.5", {"start": v(16.93, 23.24) * mm, "end": v(16.93, 12.57) * mm});
            skLineSegment(sketch, "E9.4.2.6", {"start": v(28.43, 23.24) * mm, "end": v(16.93, 23.24) * mm});
            skLineSegment(sketch, "E9.4.2.7", {"start": v(31.93, 22.29) * mm, "end": v(28.43, 22.29) * mm});
            skLineSegment(sketch, "E9.4.3.0", {"start": v(28.43, 0.63) * mm, "end": v(28.43, 1.59) * mm});
            skLineSegment(sketch, "E9.4.3.1", {"start": v(16.93, 0.63) * mm, "end": v(28.43, 0.63) * mm});
            skLineSegment(sketch, "E9.4.3.2", {"start": v(31.93, 1.59) * mm, "end": v(31.93, 10.35) * mm});
            skLineSegment(sketch, "E9.4.3.3", {"start": v(28.43, 10.35) * mm, "end": v(28.43, 11.3) * mm});
            skLineSegment(sketch, "E9.4.3.4", {"start": v(28.43, 1.59) * mm, "end": v(31.93, 1.59) * mm});
            skLineSegment(sketch, "E9.4.3.5", {"start": v(16.93, 11.3) * mm, "end": v(16.93, 0.63) * mm});
            skLineSegment(sketch, "E9.4.3.6", {"start": v(28.43, 11.3) * mm, "end": v(16.93, 11.3) * mm});
            skLineSegment(sketch, "E9.4.3.7", {"start": v(31.93, 10.35) * mm, "end": v(28.43, 10.35) * mm});
            skLineSegment(sketch, "E9.4.4.0", {"start": v(28.43, -11.3) * mm, "end": v(28.43, -10.35) * mm});
            skLineSegment(sketch, "E9.4.4.1", {"start": v(16.93, -11.3) * mm, "end": v(28.43, -11.3) * mm});
            skLineSegment(sketch, "E9.4.4.2", {"start": v(31.93, -10.35) * mm, "end": v(31.93, -1.59) * mm});
            skLineSegment(sketch, "E9.4.4.3", {"start": v(28.43, -1.59) * mm, "end": v(28.43, -0.63) * mm});
            skLineSegment(sketch, "E9.4.4.4", {"start": v(28.43, -10.35) * mm, "end": v(31.93, -10.35) * mm});
            skLineSegment(sketch, "E9.4.4.5", {"start": v(16.93, -0.63) * mm, "end": v(16.93, -11.3) * mm});
            skLineSegment(sketch, "E9.4.4.6", {"start": v(28.43, -0.63) * mm, "end": v(16.93, -0.63) * mm});
            skLineSegment(sketch, "E9.4.4.7", {"start": v(31.93, -1.59) * mm, "end": v(28.43, -1.59) * mm});
            skLineSegment(sketch, "E9.4.5.0", {"start": v(28.43, -23.24) * mm, "end": v(28.43, -22.29) * mm});
            skLineSegment(sketch, "E9.4.5.1", {"start": v(16.93, -23.24) * mm, "end": v(28.43, -23.24) * mm});
            skLineSegment(sketch, "E9.4.5.2", {"start": v(31.93, -22.29) * mm, "end": v(31.93, -13.53) * mm});
            skLineSegment(sketch, "E9.4.5.3", {"start": v(28.43, -13.53) * mm, "end": v(28.43, -12.57) * mm});
            skLineSegment(sketch, "E9.4.5.4", {"start": v(28.43, -22.29) * mm, "end": v(31.93, -22.29) * mm});
            skLineSegment(sketch, "E9.4.5.5", {"start": v(16.93, -12.57) * mm, "end": v(16.93, -23.24) * mm});
            skLineSegment(sketch, "E9.4.5.6", {"start": v(28.43, -12.57) * mm, "end": v(16.93, -12.57) * mm});
            skLineSegment(sketch, "E9.4.5.7", {"start": v(31.93, -13.53) * mm, "end": v(28.43, -13.53) * mm});
            skLineSegment(sketch, "E9.4.6.0", {"start": v(28.43, -35.18) * mm, "end": v(28.43, -34.23) * mm});
            skLineSegment(sketch, "E9.4.6.1", {"start": v(16.93, -35.18) * mm, "end": v(28.43, -35.18) * mm});
            skLineSegment(sketch, "E9.4.6.2", {"start": v(31.93, -34.23) * mm, "end": v(31.93, -25.46) * mm});
            skLineSegment(sketch, "E9.4.6.3", {"start": v(28.43, -25.46) * mm, "end": v(28.43, -24.51) * mm});
            skLineSegment(sketch, "E9.4.6.4", {"start": v(28.43, -34.23) * mm, "end": v(31.93, -34.23) * mm});
            skLineSegment(sketch, "E9.4.6.5", {"start": v(16.93, -24.51) * mm, "end": v(16.93, -35.18) * mm});
            skLineSegment(sketch, "E9.4.6.6", {"start": v(28.43, -24.51) * mm, "end": v(16.93, -24.51) * mm});
            skLineSegment(sketch, "E9.4.6.7", {"start": v(31.93, -25.46) * mm, "end": v(28.43, -25.46) * mm});
            skLineSegment(sketch, "E9.4.7.0", {"start": v(28.43, -47.12) * mm, "end": v(28.43, -46.16) * mm});
            skLineSegment(sketch, "E9.4.7.1", {"start": v(16.93, -47.12) * mm, "end": v(28.43, -47.12) * mm});
            skLineSegment(sketch, "E9.4.7.2", {"start": v(31.93, -46.16) * mm, "end": v(31.93, -37.4) * mm});
            skLineSegment(sketch, "E9.4.7.3", {"start": v(28.43, -37.4) * mm, "end": v(28.43, -36.45) * mm});
            skLineSegment(sketch, "E9.4.7.4", {"start": v(28.43, -46.16) * mm, "end": v(31.93, -46.16) * mm});
            skLineSegment(sketch, "E9.4.7.5", {"start": v(16.93, -36.45) * mm, "end": v(16.93, -47.12) * mm});
            skLineSegment(sketch, "E9.4.7.6", {"start": v(28.43, -36.45) * mm, "end": v(16.93, -36.45) * mm});
            skLineSegment(sketch, "E9.4.7.7", {"start": v(31.93, -37.4) * mm, "end": v(28.43, -37.4) * mm});
            skLineSegment(sketch, "E9.5.0.0", {"start": v(44.7, 36.45) * mm, "end": v(44.7, 37.4) * mm});
            skLineSegment(sketch, "E9.5.0.1", {"start": v(33.2, 36.45) * mm, "end": v(44.7, 36.45) * mm});
            skLineSegment(sketch, "E9.5.0.2", {"start": v(48.2, 37.4) * mm, "end": v(48.2, 46.16) * mm});
            skLineSegment(sketch, "E9.5.0.3", {"start": v(44.7, 46.16) * mm, "end": v(44.7, 47.12) * mm});
            skLineSegment(sketch, "E9.5.0.4", {"start": v(44.7, 37.4) * mm, "end": v(48.2, 37.4) * mm});
            skLineSegment(sketch, "E9.5.0.5", {"start": v(33.2, 47.12) * mm, "end": v(33.2, 36.45) * mm});
            skLineSegment(sketch, "E9.5.0.6", {"start": v(44.7, 47.12) * mm, "end": v(33.2, 47.12) * mm});
            skLineSegment(sketch, "E9.5.0.7", {"start": v(48.2, 46.16) * mm, "end": v(44.7, 46.16) * mm});
            skLineSegment(sketch, "E9.5.1.0", {"start": v(44.7, 24.5) * mm, "end": v(44.7, 25.46) * mm});
            skLineSegment(sketch, "E9.5.1.1", {"start": v(33.2, 24.5) * mm, "end": v(44.7, 24.5) * mm});
            skLineSegment(sketch, "E9.5.1.2", {"start": v(48.2, 25.46) * mm, "end": v(48.2, 34.23) * mm});
            skLineSegment(sketch, "E9.5.1.3", {"start": v(44.7, 34.23) * mm, "end": v(44.7, 35.18) * mm});
            skLineSegment(sketch, "E9.5.1.4", {"start": v(44.7, 25.46) * mm, "end": v(48.2, 25.46) * mm});
            skLineSegment(sketch, "E9.5.1.5", {"start": v(33.2, 35.18) * mm, "end": v(33.2, 24.5) * mm});
            skLineSegment(sketch, "E9.5.1.6", {"start": v(44.7, 35.18) * mm, "end": v(33.2, 35.18) * mm});
            skLineSegment(sketch, "E9.5.1.7", {"start": v(48.2, 34.23) * mm, "end": v(44.7, 34.23) * mm});
            skLineSegment(sketch, "E9.5.2.0", {"start": v(44.7, 12.57) * mm, "end": v(44.7, 13.53) * mm});
            skLineSegment(sketch, "E9.5.2.1", {"start": v(33.2, 12.57) * mm, "end": v(44.7, 12.57) * mm});
            skLineSegment(sketch, "E9.5.2.2", {"start": v(48.2, 13.53) * mm, "end": v(48.2, 22.29) * mm});
            skLineSegment(sketch, "E9.5.2.3", {"start": v(44.7, 22.29) * mm, "end": v(44.7, 23.24) * mm});
            skLineSegment(sketch, "E9.5.2.4", {"start": v(44.7, 13.53) * mm, "end": v(48.2, 13.53) * mm});
            skLineSegment(sketch, "E9.5.2.5", {"start": v(33.2, 23.24) * mm, "end": v(33.2, 12.57) * mm});
            skLineSegment(sketch, "E9.5.2.6", {"start": v(44.7, 23.24) * mm, "end": v(33.2, 23.24) * mm});
            skLineSegment(sketch, "E9.5.2.7", {"start": v(48.2, 22.29) * mm, "end": v(44.7, 22.29) * mm});
            skLineSegment(sketch, "E9.5.3.0", {"start": v(44.7, 0.63) * mm, "end": v(44.7, 1.59) * mm});
            skLineSegment(sketch, "E9.5.3.1", {"start": v(33.2, 0.63) * mm, "end": v(44.7, 0.63) * mm});
            skLineSegment(sketch, "E9.5.3.2", {"start": v(48.2, 1.59) * mm, "end": v(48.2, 10.35) * mm});
            skLineSegment(sketch, "E9.5.3.3", {"start": v(44.7, 10.35) * mm, "end": v(44.7, 11.3) * mm});
            skLineSegment(sketch, "E9.5.3.4", {"start": v(44.7, 1.59) * mm, "end": v(48.2, 1.59) * mm});
            skLineSegment(sketch, "E9.5.3.5", {"start": v(33.2, 11.3) * mm, "end": v(33.2, 0.63) * mm});
            skLineSegment(sketch, "E9.5.3.6", {"start": v(44.7, 11.3) * mm, "end": v(33.2, 11.3) * mm});
            skLineSegment(sketch, "E9.5.3.7", {"start": v(48.2, 10.35) * mm, "end": v(44.7, 10.35) * mm});
            skLineSegment(sketch, "E9.5.4.0", {"start": v(44.7, -11.3) * mm, "end": v(44.7, -10.35) * mm});
            skLineSegment(sketch, "E9.5.4.1", {"start": v(33.2, -11.3) * mm, "end": v(44.7, -11.3) * mm});
            skLineSegment(sketch, "E9.5.4.2", {"start": v(48.2, -10.35) * mm, "end": v(48.2, -1.59) * mm});
            skLineSegment(sketch, "E9.5.4.3", {"start": v(44.7, -1.59) * mm, "end": v(44.7, -0.63) * mm});
            skLineSegment(sketch, "E9.5.4.4", {"start": v(44.7, -10.35) * mm, "end": v(48.2, -10.35) * mm});
            skLineSegment(sketch, "E9.5.4.5", {"start": v(33.2, -0.63) * mm, "end": v(33.2, -11.3) * mm});
            skLineSegment(sketch, "E9.5.4.6", {"start": v(44.7, -0.63) * mm, "end": v(33.2, -0.63) * mm});
            skLineSegment(sketch, "E9.5.4.7", {"start": v(48.2, -1.59) * mm, "end": v(44.7, -1.59) * mm});
            skLineSegment(sketch, "E9.5.5.0", {"start": v(44.7, -23.24) * mm, "end": v(44.7, -22.29) * mm});
            skLineSegment(sketch, "E9.5.5.1", {"start": v(33.2, -23.24) * mm, "end": v(44.7, -23.24) * mm});
            skLineSegment(sketch, "E9.5.5.2", {"start": v(48.2, -22.29) * mm, "end": v(48.2, -13.53) * mm});
            skLineSegment(sketch, "E9.5.5.3", {"start": v(44.7, -13.53) * mm, "end": v(44.7, -12.57) * mm});
            skLineSegment(sketch, "E9.5.5.4", {"start": v(44.7, -22.29) * mm, "end": v(48.2, -22.29) * mm});
            skLineSegment(sketch, "E9.5.5.5", {"start": v(33.2, -12.57) * mm, "end": v(33.2, -23.24) * mm});
            skLineSegment(sketch, "E9.5.5.6", {"start": v(44.7, -12.57) * mm, "end": v(33.2, -12.57) * mm});
            skLineSegment(sketch, "E9.5.5.7", {"start": v(48.2, -13.53) * mm, "end": v(44.7, -13.53) * mm});
            skLineSegment(sketch, "E9.5.6.0", {"start": v(44.7, -35.18) * mm, "end": v(44.7, -34.23) * mm});
            skLineSegment(sketch, "E9.5.6.1", {"start": v(33.2, -35.18) * mm, "end": v(44.7, -35.18) * mm});
            skLineSegment(sketch, "E9.5.6.2", {"start": v(48.2, -34.23) * mm, "end": v(48.2, -25.46) * mm});
            skLineSegment(sketch, "E9.5.6.3", {"start": v(44.7, -25.46) * mm, "end": v(44.7, -24.51) * mm});
            skLineSegment(sketch, "E9.5.6.4", {"start": v(44.7, -34.23) * mm, "end": v(48.2, -34.23) * mm});
            skLineSegment(sketch, "E9.5.6.5", {"start": v(33.2, -24.51) * mm, "end": v(33.2, -35.18) * mm});
            skLineSegment(sketch, "E9.5.6.6", {"start": v(44.7, -24.51) * mm, "end": v(33.2, -24.51) * mm});
            skLineSegment(sketch, "E9.5.6.7", {"start": v(48.2, -25.46) * mm, "end": v(44.7, -25.46) * mm});
            skLineSegment(sketch, "E9.5.7.0", {"start": v(44.7, -47.12) * mm, "end": v(44.7, -46.16) * mm});
            skLineSegment(sketch, "E9.5.7.1", {"start": v(33.2, -47.12) * mm, "end": v(44.7, -47.12) * mm});
            skLineSegment(sketch, "E9.5.7.2", {"start": v(48.2, -46.16) * mm, "end": v(48.2, -37.4) * mm});
            skLineSegment(sketch, "E9.5.7.3", {"start": v(44.7, -37.4) * mm, "end": v(44.7, -36.45) * mm});
            skLineSegment(sketch, "E9.5.7.4", {"start": v(44.7, -46.16) * mm, "end": v(48.2, -46.16) * mm});
            skLineSegment(sketch, "E9.5.7.5", {"start": v(33.2, -36.45) * mm, "end": v(33.2, -47.12) * mm});
            skLineSegment(sketch, "E9.5.7.6", {"start": v(44.7, -36.45) * mm, "end": v(33.2, -36.45) * mm});
            skLineSegment(sketch, "E9.5.7.7", {"start": v(48.2, -37.4) * mm, "end": v(44.7, -37.4) * mm});
            skLineSegment(sketch, "E9.direction1", {"start": v(-48.2, 47.12) * mm, "end": v(-31.92, 47.12) * mm, "construction": true});
            skLineSegment(sketch, "E9.direction2", {"start": v(-48.2, 47.12) * mm, "end": v(-48.2, 35.18) * mm, "construction": true});
            skSolve(sketch);
        }
        {
            var Q0;
            Q0=makeQuery(id+"F0.imprint","IMPRINT",FACE,{"disambiguationData":[TD([[makeQuery(id+"F0.imprint","IMPRINT",EDGE,{"derivedFrom":sQuery(id+"F0.wireOp",EDGE,"E0.bottom")}),-1.0]])]});
            extrude(context, id + "F1", {"entities" : qUnion([Q0]), "depth" : 5 * mm});
        }
        {
            var Q0;
            Q0=makeQuery(id+"F0.imprint","IMPRINT",FACE,{"disambiguationData":[TD([[makeQuery(id+"F0.imprint","IMPRINT",EDGE,{"derivedFrom":sQuery(id+"F0.wireOp",EDGE,"E9.2.5.0")}),1.0]])]});
            var Q1;
            Q1=makeQuery(id+"F0.imprint","IMPRINT",FACE,{"disambiguationData":[TD([[makeQuery(id+"F0.imprint","IMPRINT",EDGE,{"derivedFrom":sQuery(id+"F0.wireOp",EDGE,"E9.4.4.0")}),1.0]])]});
            var Q2;
            Q2=makeQuery(id+"F0.imprint","IMPRINT",FACE,{"disambiguationData":[TD([[makeQuery(id+"F0.imprint","IMPRINT",EDGE,{"derivedFrom":sQuery(id+"F0.wireOp",EDGE,"E9.1.2.0")}),1.0]])]});
            var Q3;
            Q3=makeQuery(id+"F0.imprint","IMPRINT",FACE,{"disambiguationData":[TD([[makeQuery(id+"F0.imprint","IMPRINT",EDGE,{"derivedFrom":sQuery(id+"F0.wireOp",EDGE,"E9.3.6.0")}),1.0]])]});
            var Q4;
            Q4=makeQuery(id+"F0.imprint","IMPRINT",FACE,{"disambiguationData":[TD([[makeQuery(id+"F0.imprint","IMPRINT",EDGE,{"derivedFrom":sQuery(id+"F0.wireOp",EDGE,"E9.2.1.0")}),1.0]])]});
            var Q5;
            Q5=makeQuery(id+"F0.imprint","IMPRINT",FACE,{"disambiguationData":[TD([[makeQuery(id+"F0.imprint","IMPRINT",EDGE,{"derivedFrom":sQuery(id+"F0.wireOp",EDGE,"E9.5.0.0")}),1.0]])]});
            var Q6;
            Q6=makeQuery(id+"F0.imprint","IMPRINT",FACE,{"disambiguationData":[TD([[makeQuery(id+"F0.imprint","IMPRINT",EDGE,{"derivedFrom":sQuery(id+"F0.wireOp",EDGE,"E9.0.7.0")}),1.0]])]});
            var Q7;
            Q7=makeQuery(id+"F0.imprint","IMPRINT",FACE,{"disambiguationData":[TD([[makeQuery(id+"F0.imprint","IMPRINT",EDGE,{"derivedFrom":sQuery(id+"F0.wireOp",EDGE,"E9.0.2.0")}),1.0]])]});
            var Q8;
            Q8=makeQuery(id+"F0.imprint","IMPRINT",FACE,{"disambiguationData":[TD([[makeQuery(id+"F0.imprint","IMPRINT",EDGE,{"derivedFrom":sQuery(id+"F0.wireOp",EDGE,"E9.4.5.0")}),1.0]])]});
            var Q9;
            Q9=makeQuery(id+"F0.imprint","IMPRINT",FACE,{"disambiguationData":[TD([[makeQuery(id+"F0.imprint","IMPRINT",EDGE,{"derivedFrom":sQuery(id+"F0.wireOp",EDGE,"E9.5.3.0")}),1.0]])]});
            var Q10;
            Q10=makeQuery(id+"F0.imprint","IMPRINT",FACE,{"disambiguationData":[TD([[makeQuery(id+"F0.imprint","IMPRINT",EDGE,{"derivedFrom":sQuery(id+"F0.wireOp",EDGE,"E9.3.1.0")}),1.0]])]});
            var Q11;
            Q11=makeQuery(id+"F0.imprint","IMPRINT",FACE,{"disambiguationData":[TD([[makeQuery(id+"F0.imprint","IMPRINT",EDGE,{"derivedFrom":sQuery(id+"F0.wireOp",EDGE,"E9.4.1.0")}),1.0]])]});
            var Q12;
            Q12=makeQuery(id+"F0.imprint","IMPRINT",FACE,{"disambiguationData":[TD([[makeQuery(id+"F0.imprint","IMPRINT",EDGE,{"derivedFrom":sQuery(id+"F0.wireOp",EDGE,"E9.4.3.0")}),1.0]])]});
            var Q13;
            Q13=makeQuery(id+"F0.imprint","IMPRINT",FACE,{"disambiguationData":[TD([[makeQuery(id+"F0.imprint","IMPRINT",EDGE,{"derivedFrom":sQuery(id+"F0.wireOp",EDGE,"E9.1.5.0")}),1.0]])]});
            var Q14;
            Q14=makeQuery(id+"F0.imprint","IMPRINT",FACE,{"disambiguationData":[TD([[makeQuery(id+"F0.imprint","IMPRINT",EDGE,{"derivedFrom":sQuery(id+"F0.wireOp",EDGE,"E9.0.6.0")}),1.0]])]});
            var Q15;
            Q15=makeQuery(id+"F0.imprint","IMPRINT",FACE,{"disambiguationData":[TD([[makeQuery(id+"F0.imprint","IMPRINT",EDGE,{"derivedFrom":sQuery(id+"F0.wireOp",EDGE,"E9.2.4.0")}),1.0]])]});
            var Q16;
            Q16=makeQuery(id+"F0.imprint","IMPRINT",FACE,{"disambiguationData":[TD([[makeQuery(id+"F0.imprint","IMPRINT",EDGE,{"derivedFrom":sQuery(id+"F0.wireOp",EDGE,"E9.0.4.0")}),1.0]])]});
            var Q17;
            Q17=makeQuery(id+"F0.imprint","IMPRINT",FACE,{"disambiguationData":[TD([[makeQuery(id+"F0.imprint","IMPRINT",EDGE,{"derivedFrom":sQuery(id+"F0.wireOp",EDGE,"E9.0.3.0")}),1.0]])]});
            var Q18;
            Q18=makeQuery(id+"F0.imprint","IMPRINT",FACE,{"disambiguationData":[TD([[makeQuery(id+"F0.imprint","IMPRINT",EDGE,{"derivedFrom":sQuery(id+"F0.wireOp",EDGE,"E9.5.4.0")}),1.0]])]});
            var Q19;
            Q19=makeQuery(id+"F0.imprint","IMPRINT",FACE,{"disambiguationData":[TD([[makeQuery(id+"F0.imprint","IMPRINT",EDGE,{"derivedFrom":sQuery(id+"F0.wireOp",EDGE,"E9.1.4.0")}),1.0]])]});
            var Q20;
            Q20=makeQuery(id+"F0.imprint","IMPRINT",FACE,{"disambiguationData":[TD([[makeQuery(id+"F0.imprint","IMPRINT",EDGE,{"derivedFrom":sQuery(id+"F0.wireOp",EDGE,"E9.4.6.0")}),1.0]])]});
            var Q21;
            Q21=makeQuery(id+"F0.imprint","IMPRINT",FACE,{"disambiguationData":[TD([[makeQuery(id+"F0.imprint","IMPRINT",EDGE,{"derivedFrom":sQuery(id+"F0.wireOp",EDGE,"E9.3.2.0")}),1.0]])]});
            var Q22;
            Q22=makeQuery(id+"F0.imprint","IMPRINT",FACE,{"disambiguationData":[TD([[makeQuery(id+"F0.imprint","IMPRINT",EDGE,{"derivedFrom":sQuery(id+"F0.wireOp",EDGE,"E9.1.6.0")}),1.0]])]});
            var Q23;
            Q23=makeQuery(id+"F0.imprint","IMPRINT",FACE,{"disambiguationData":[TD([[makeQuery(id+"F0.imprint","IMPRINT",EDGE,{"derivedFrom":sQuery(id+"F0.wireOp",EDGE,"E9.3.0.0")}),1.0]])]});
            var Q24;
            Q24=makeQuery(id+"F0.imprint","IMPRINT",FACE,{"disambiguationData":[TD([[makeQuery(id+"F0.imprint","IMPRINT",EDGE,{"derivedFrom":sQuery(id+"F0.wireOp",EDGE,"E9.5.2.0")}),1.0]])]});
            var Q25;
            Q25=makeQuery(id+"F0.imprint","IMPRINT",FACE,{"disambiguationData":[TD([[makeQuery(id+"F0.imprint","IMPRINT",EDGE,{"derivedFrom":sQuery(id+"F0.wireOp",EDGE,"E9.2.7.0")}),1.0]])]});
            var Q26;
            Q26=makeQuery(id+"F0.imprint","IMPRINT",FACE,{"disambiguationData":[TD([[makeQuery(id+"F0.imprint","IMPRINT",EDGE,{"derivedFrom":sQuery(id+"F0.wireOp",EDGE,"E9.3.3.0")}),1.0]])]});
            var Q27;
            Q27=makeQuery(id+"F0.imprint","IMPRINT",FACE,{"disambiguationData":[TD([[makeQuery(id+"F0.imprint","IMPRINT",EDGE,{"derivedFrom":sQuery(id+"F0.wireOp",EDGE,"E9.5.1.0")}),1.0]])]});
            var Q28;
            Q28=makeQuery(id+"F0.imprint","IMPRINT",FACE,{"disambiguationData":[TD([[makeQuery(id+"F0.imprint","IMPRINT",EDGE,{"derivedFrom":sQuery(id+"F0.wireOp",EDGE,"E9.1.7.0")}),1.0]])]});
            var Q29;
            Q29=makeQuery(id+"F0.imprint","IMPRINT",FACE,{"disambiguationData":[TD([[makeQuery(id+"F0.imprint","IMPRINT",EDGE,{"derivedFrom":sQuery(id+"F0.wireOp",EDGE,"E9.1.0.0")}),1.0]])]});
            var Q30;
            Q30=makeQuery(id+"F0.imprint","IMPRINT",FACE,{"disambiguationData":[TD([[makeQuery(id+"F0.imprint","IMPRINT",EDGE,{"derivedFrom":sQuery(id+"F0.wireOp",EDGE,"E9.5.6.0")}),1.0]])]});
            var Q31;
            Q31=makeQuery(id+"F0.imprint","IMPRINT",FACE,{"disambiguationData":[TD([[makeQuery(id+"F0.imprint","IMPRINT",EDGE,{"derivedFrom":sQuery(id+"F0.wireOp",EDGE,"E9.0.5.0")}),1.0]])]});
            var Q32;
            Q32=makeQuery(id+"F0.imprint","IMPRINT",FACE,{"disambiguationData":[TD([[makeQuery(id+"F0.imprint","IMPRINT",EDGE,{"derivedFrom":sQuery(id+"F0.wireOp",EDGE,"E9.4.7.0")}),1.0]])]});
            var Q33;
            Q33=makeQuery(id+"F0.imprint","IMPRINT",FACE,{"disambiguationData":[TD([[makeQuery(id+"F0.imprint","IMPRINT",EDGE,{"derivedFrom":sQuery(id+"F0.wireOp",EDGE,"E9.4.0.0")}),1.0]])]});
            var Q34;
            Q34=makeQuery(id+"F0.imprint","IMPRINT",FACE,{"disambiguationData":[TD([[makeQuery(id+"F0.imprint","IMPRINT",EDGE,{"derivedFrom":sQuery(id+"F0.wireOp",EDGE,"E9.5.5.0")}),1.0]])]});
            var Q35;
            Q35=makeQuery(id+"F0.imprint","IMPRINT",FACE,{"disambiguationData":[TD([[makeQuery(id+"F0.imprint","IMPRINT",EDGE,{"derivedFrom":sQuery(id+"F0.wireOp",EDGE,"E9.5.7.0")}),1.0]])]});
            var Q36;
            Q36=makeQuery(id+"F0.imprint","IMPRINT",FACE,{"disambiguationData":[TD([[makeQuery(id+"F0.imprint","IMPRINT",EDGE,{"derivedFrom":sQuery(id+"F0.wireOp",EDGE,"E9.1.3.0")}),1.0]])]});
            var Q37;
            Q37=makeQuery(id+"F0.imprint","IMPRINT",FACE,{"disambiguationData":[TD([[makeQuery(id+"F0.imprint","IMPRINT",EDGE,{"derivedFrom":sQuery(id+"F0.wireOp",EDGE,"E9.2.3.0")}),1.0]])]});
            var Q38;
            Q38=makeQuery(id+"F0.imprint","IMPRINT",FACE,{"disambiguationData":[TD([[makeQuery(id+"F0.imprint","IMPRINT",EDGE,{"derivedFrom":sQuery(id+"F0.wireOp",EDGE,"E9.1.1.0")}),1.0]])]});
            var Q39;
            Q39=makeQuery(id+"F0.imprint","IMPRINT",FACE,{"disambiguationData":[TD([[makeQuery(id+"F0.imprint","IMPRINT",EDGE,{"derivedFrom":sQuery(id+"F0.wireOp",EDGE,"E9.4.2.0")}),1.0]])]});
            var Q40;
            Q40=makeQuery(id+"F0.imprint","IMPRINT",FACE,{"disambiguationData":[TD([[makeQuery(id+"F0.imprint","IMPRINT",EDGE,{"derivedFrom":sQuery(id+"F0.wireOp",EDGE,"E9.3.4.0")}),1.0]])]});
            var Q41;
            Q41=makeQuery(id+"F0.imprint","IMPRINT",FACE,{"disambiguationData":[TD([[makeQuery(id+"F0.imprint","IMPRINT",EDGE,{"derivedFrom":sQuery(id+"F0.wireOp",EDGE,"E9.0.1.0")}),1.0]])]});
            var Q42;
            Q42=makeQuery(id+"F0.imprint","IMPRINT",FACE,{"disambiguationData":[TD([[makeQuery(id+"F0.imprint","IMPRINT",EDGE,{"derivedFrom":sQuery(id+"F0.wireOp",EDGE,"E9.2.2.0")}),1.0]])]});
            var Q43;
            Q43=makeQuery(id+"F0.imprint","IMPRINT",FACE,{"disambiguationData":[TD([[makeQuery(id+"F0.imprint","IMPRINT",EDGE,{"derivedFrom":sQuery(id+"F0.wireOp",EDGE,"E9.3.7.0")}),1.0]])]});
            var Q44;
            Q44=makeQuery(id+"F0.imprint","IMPRINT",FACE,{"disambiguationData":[TD([[makeQuery(id+"F0.imprint","IMPRINT",EDGE,{"derivedFrom":sQuery(id+"F0.wireOp",EDGE,"E9.2.6.0")}),1.0]])]});
            var Q45;
            Q45=makeQuery(id+"F0.imprint","IMPRINT",FACE,{"disambiguationData":[TD([[makeQuery(id+"F0.imprint","IMPRINT",EDGE,{"derivedFrom":sQuery(id+"F0.wireOp",EDGE,"E1")}),1.0]])]});
            var Q46;
            Q46=makeQuery(id+"F0.imprint","IMPRINT",FACE,{"disambiguationData":[TD([[makeQuery(id+"F0.imprint","IMPRINT",EDGE,{"derivedFrom":sQuery(id+"F0.wireOp",EDGE,"E9.2.0.0")}),1.0]])]});
            var Q47;
            Q47=makeQuery(id+"F0.imprint","IMPRINT",FACE,{"disambiguationData":[TD([[makeQuery(id+"F0.imprint","IMPRINT",EDGE,{"derivedFrom":sQuery(id+"F0.wireOp",EDGE,"E9.3.5.0")}),1.0]])]});
            extrude(context, id + "F2", {"entities" : qUnion([Q0, Q1, Q2, Q3, Q4, Q5, Q6, Q7, Q8, Q9, Q10, Q11, Q12, Q13, Q14, Q15, Q16, Q17, Q18, Q19, Q20, Q21, Q22, Q23, Q24, Q25, Q26, Q27, Q28, Q29, Q30, Q31, Q32, Q33, Q34, Q35, Q36, Q37, Q38, Q39, Q40, Q41, Q42, Q43, Q44, Q45, Q46, Q47]), "operationType" : NewBodyOperationType.ADD, "depth" : 2.5 * mm});
        }
    });
